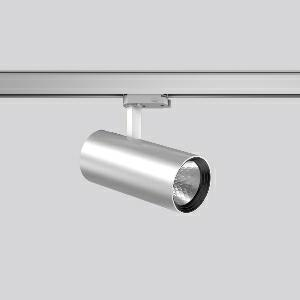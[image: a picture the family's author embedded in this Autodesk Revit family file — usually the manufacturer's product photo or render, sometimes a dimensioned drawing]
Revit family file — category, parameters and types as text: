
# Revit family: deecos_s_mini_742196_004_3_2cd6
name_source: partatom
category: Lighting Fixtures
units: mm (PartAtom-declared; Revit-internal decimal feet)

## family parameters
Cut with Voids When Loaded = No
Host = Face
Light Source = No
Part Type = Normal
Room Calculation Point = No
Round Connector Dimension = Use Diameter
Shared = No

## types (1)
- DEECOS S mini (1 x LED Modul 935, 2500 lm, 3500)
    Apparent Load = 20 VA
    Approval mark = CE
    CIE Flux Codes = 99 100 100 100 100
    Color Rendering = 92
    Color Temperature = 3500
    Default Elevation = 1800 mm
    Description = Series: DEECOS S mini
LED surface-mounted projector in modern design with no visible cooling ribs. Housing: die-cast aluminium, powder-coated. Rotation range: 356°. Swivel range: 90°. Black plastic ring and recessed LED to prevent glare from the side. Optical assembly with reflector made of MIRO-Silver with 98% total light reflection for outstanding efficiency - can be changed without tools. Best colour rendering index Ra>90. With multi adaptor for 3-circuit tracks 230 V. Suitable for Track on ceiling, Wall track. High quality converter without flickering and stroboscopic effect. The following accessories can be mounted without use of tools: interchangeable lenses, decorative glasses, honeycomb louvre, clear and frosted diffusers, white interchangeable plastic ring. 
Colour: silver
Diameter: 87 mm
Height: 214 mm
Lamp: LED
Socket: without socket
Colour temperature: 3500K
Colour rendering index (CRI): 92
System power: 20 W
Rated luminous flux: 2500 lm
Luminous efficiency: 125 lm/W
Control gear: Regulated power supply
Protection class: I
Type of protection: IP 20
    Height = 214 mm
    Lamp = 1 x LED Modul 935
    Lamp Light Flux = 2500 lm
    Lamp count = 1
    Length = 87 mm
    Lifetime = 50000 h
    Luminous efficacy = 125 lm/W
    Manufacturer = RZB
    ModVariant = No
    Model = 742196.004.3
    Mounting Place = Ceiling
    Mounting Type = Rail mounted
    Number of Poles = 1
    OnlyDefault = Yes
    Power Factor = 1
    Product Name = DEECOS S mini
    Product group = Track mounted projectors
    ProductGroupID = 301
    Protection Class = Protection class I
    Protection Degree = IP 20
    RLX_Detail_Level = 1
    RLX_Emergency_Light_Flux = 0 lm
    RLX_Emergency_Type = 0
    RLX_Emergency_Type_DB = No
    RlxData = <blob elided: 37301 chars, md5=6d7c3c6d>
    Socket = socket
    Standby Power = 0 W
    System Light Flux = 2500 lm
    System Power = 20 W
    Type Comments = Product without accessories
    Type Image = 741926.004.jpg
    URL = http://relux.com
    VarID = ---
    Voltage = 230 V
    Voltage Range = 220-240 V
    Weight = 0.00 kg
    Width = 0 mm  [stored 0 ft]

note: [stored X ft] marks values corroborated as IEEE doubles in the binary element streams (Revit-internal decimal feet)

## geometry (parser evidence)
native form markers: Blend x4, Sweep x11
no freeform markers — native parametric forms only
